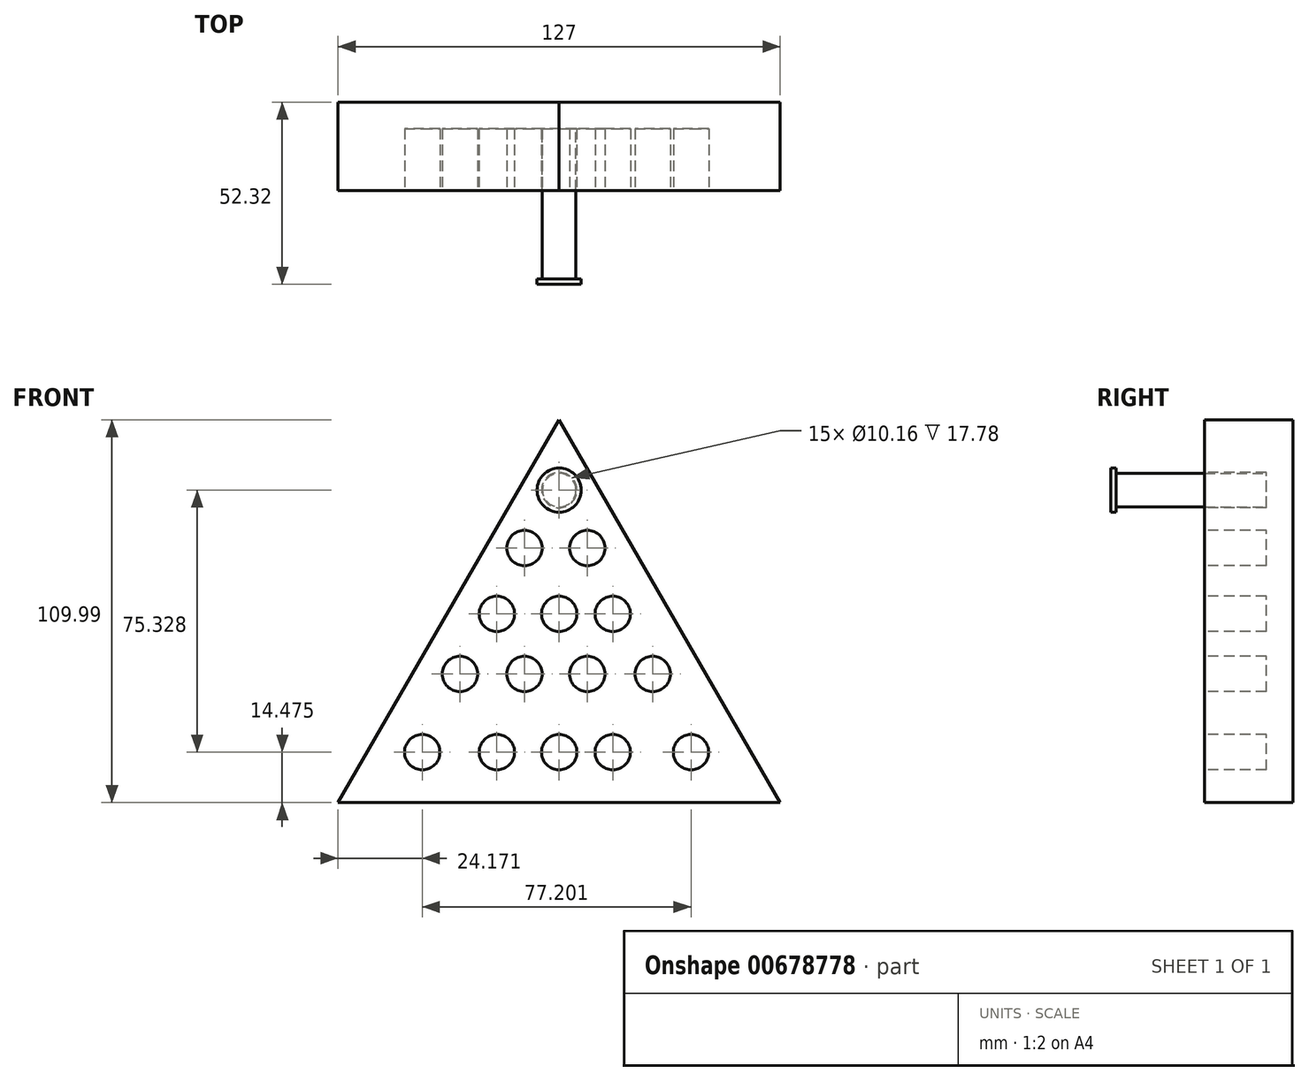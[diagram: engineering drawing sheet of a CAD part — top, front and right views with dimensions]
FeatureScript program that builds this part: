
annotation { "Feature Type Name" : "Feature", "Feature Type Description" : "" }
export const myFeature = defineFeature(function(context is Context, id is Id, definition is map)
    precondition{}
    {
        {
            var Q0;
            Q0=qCreatedBy(makeId("Front.planeOp"),FACE);
            var sketch = newSketch(context, id + "F0", { "sketchPlane" : qUnion([Q0])});
            skLineSegment(sketch, "E0", {"start": v(0, 55.77) * mm, "end": v(-63.5, -54.22) * mm});
            skLineSegment(sketch, "E1", {"start": v(-63.5, -54.22) * mm, "end": v(63.5, -54.22) * mm});
            skLineSegment(sketch, "E2", {"start": v(0, 55.77) * mm, "end": v(63.5, -54.22) * mm});
            skSolve(sketch);
        }
        {
            var Q0;
            Q0 = qSketchRegion(id + "F0", true);
            extrude(context, id + "F1", {"entities" : qUnion([Q0]), "depth" : 25.4 * mm, "offsetDistance" : 25.4 * mm});
        }
        {
            var Q0;
            Q0=makeQuery(id+"F1.opExtrude","CAP_FACE",FACE,{"disambiguationData":[OSD([sQuery(id+"F0.wireOp",EDGE,"E0"),sQuery(id+"F0.wireOp",EDGE,"E1"),sQuery(id+"F0.wireOp",EDGE,"E2")])],"isStart":false});
            var sketch = newSketch(context, id + "F2", { "sketchPlane" : qUnion([Q0])});
            skCircle(sketch, "E3", {"center": v(0, 35.58) * mm, "radius": 5.08 * mm});
            skCircle(sketch, "E4", {"center": v(-9.99, 18.94) * mm, "radius": 5.08 * mm});
            skCircle(sketch, "E5", {"center": v(8.12, 18.94) * mm, "radius": 5.08 * mm});
            skCircle(sketch, "E6", {"center": v(-17.9, 0) * mm, "radius": 5.08 * mm});
            skCircle(sketch, "E7", {"center": v(0, 0) * mm, "radius": 5.08 * mm});
            skCircle(sketch, "E8", {"center": v(15.4, 0) * mm, "radius": 5.08 * mm});
            skCircle(sketch, "E9", {"center": v(-28.5, -17.27) * mm, "radius": 5.08 * mm});
            skCircle(sketch, "E10", {"center": v(-9.99, -17.27) * mm, "radius": 5.08 * mm});
            skCircle(sketch, "E11", {"center": v(8.12, -17.27) * mm, "radius": 5.08 * mm});
            skCircle(sketch, "E12", {"center": v(26.84, -17.27) * mm, "radius": 5.08 * mm});
            skCircle(sketch, "E13", {"center": v(-39.33, -39.74) * mm, "radius": 5.08 * mm});
            skCircle(sketch, "E14", {"center": v(-17.9, -39.74) * mm, "radius": 5.08 * mm});
            skCircle(sketch, "E15", {"center": v(0, -39.74) * mm, "radius": 5.08 * mm});
            skPoint(sketch, "E15.centerSnap0", {"position": v(0, -54.22) * mm});
            skCircle(sketch, "E16", {"center": v(15.4, -39.74) * mm, "radius": 5.08 * mm});
            skCircle(sketch, "E17", {"center": v(37.87, -39.74) * mm, "radius": 5.08 * mm});
            skSolve(sketch);
        }
        {
            var Q0;
            Q0 = qSketchRegion(id + "F2", true);
            extrude(context, id + "F3", {"entities" : qUnion([Q0]), "operationType" : NewBodyOperationType.REMOVE, "oppositeDirection" : true, "depth" : 17.78 * mm, "offsetDistance" : 25.4 * mm});
        }
        {
            var Q0;
            Q0=makeQuery(id+"F3.boolean.opBoolean","COPY",FACE,{"derivedFrom":makeQuery(id+"F3.opExtrude","CAP_FACE",FACE,{"disambiguationData":[OSD([sQuery(id+"F2.wireOp",EDGE,"E3")])],"isStart":false})});
            var sketch = newSketch(context, id + "F4", { "sketchPlane" : qUnion([Q0])});
            skCircle(sketch, "E18", {"center": v(0, 35.58) * mm, "radius": 4.83 * mm});
            skSolve(sketch);
        }
        {
            var Q0;
            Q0 = qSketchRegion(id + "F4", true);
            extrude(context, id + "F5", {"entities" : qUnion([Q0]), "depth" : 43.18 * mm, "offsetDistance" : 25.4 * mm});
        }
        {
            var Q0;
            Q0=makeQuery(id+"F5.opExtrude","CAP_FACE",FACE,{"disambiguationData":[OSD([sQuery(id+"F4.wireOp",EDGE,"E18")])],"isStart":false});
            var sketch = newSketch(context, id + "F6", { "sketchPlane" : qUnion([Q0])});
            skCircle(sketch, "E19", {"center": v(0, 35.58) * mm, "radius": 6.35 * mm});
            skSolve(sketch);
        }
        {
            var Q0;
            Q0 = qSketchRegion(id + "F6", true);
            extrude(context, id + "F7", {"entities" : qUnion([Q0]), "operationType" : NewBodyOperationType.ADD, "depth" : 1.52 * mm, "offsetDistance" : 25.4 * mm});
        }
    });
